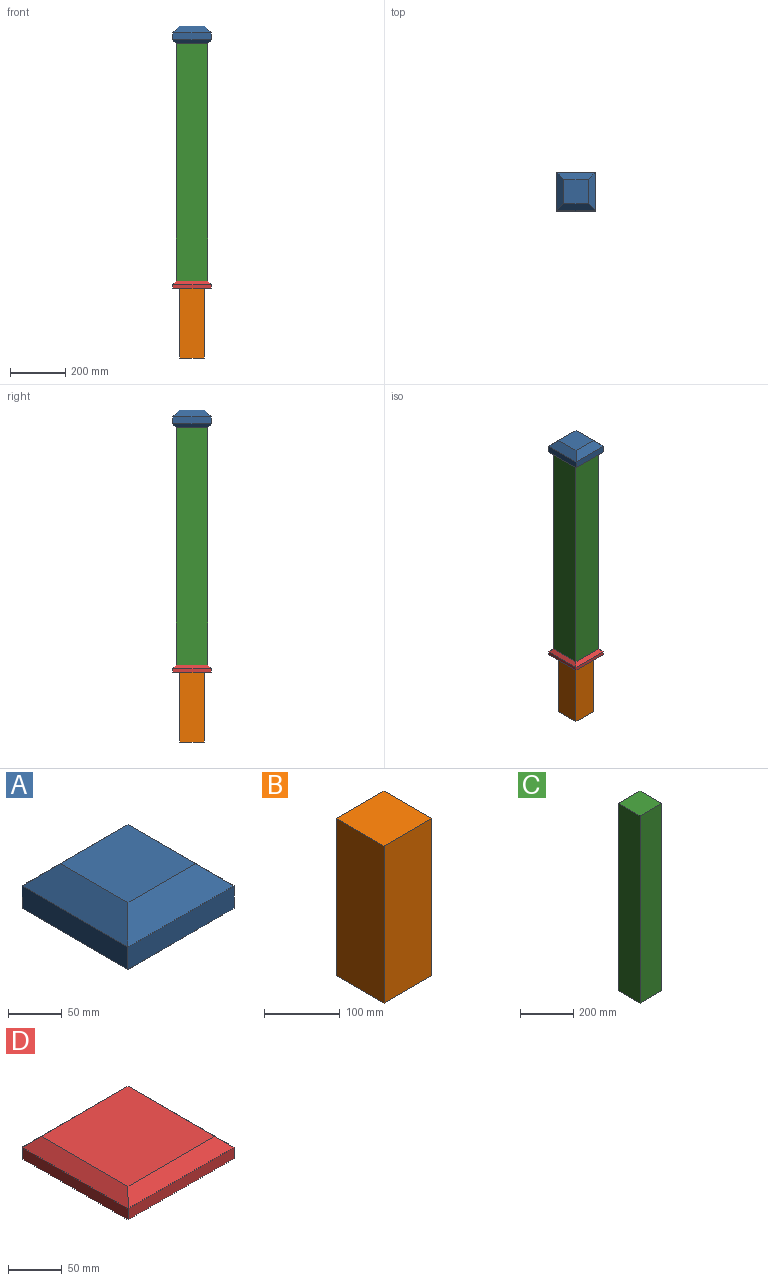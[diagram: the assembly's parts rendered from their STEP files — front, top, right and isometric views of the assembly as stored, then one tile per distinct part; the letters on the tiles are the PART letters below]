
ASSEMBLY  parts=4 mates=3
PART A: 14 faces, bbox 139.7x139.7x63.5 mm
  f0: plane 139.7x25.4mm, normal (1,0,0), area 3548.4mm2, adj f1,f3,f9,f13
  f1: plane 139.7x25.4mm, normal (0,1,0), area 3548.4mm2, adj f0,f2,f7,f11
  f2: plane 139.7x25.4mm, normal (-1,0,0), area 3548.4mm2, adj f1,f3,f6,f10
  f3: plane 139.7x25.4mm, normal (0,-1,0), area 3548.4mm2, adj f0,f2,f8,f12
  f4: plane 88.9x88.9mm, normal (0,0,1), area 7903.2mm2, adj f10,f11,f12,f13
  f5: plane 114.3x114.3mm, normal (0,0,-1), area 13064.5mm2, adj f6,f7,f8,f9
  f6: plane 139.7x12.7mm, normal (-0.71,0,-0.71), area 2281mm2, adj f2,f5,f7,f8
  f7: plane 139.7x12.7mm, normal (0,0.71,-0.71), area 2281mm2, adj f1,f5,f6,f9
  f8: plane 139.7x12.7mm, normal (0,-0.71,-0.71), area 2281mm2, adj f3,f5,f6,f9
  f9: plane 139.7x12.7mm, normal (0.71,0,-0.71), area 2281mm2, adj f0,f5,f7,f8
  f10: plane 139.7x25.4mm, normal (-0.71,0,0.71), area 4105.8mm2, adj f2,f4,f11,f12
  f11: plane 139.7x25.4mm, normal (0,0.71,0.71), area 4105.8mm2, adj f1,f4,f10,f13
  f12: plane 139.7x25.4mm, normal (0,-0.71,0.71), area 4105.8mm2, adj f3,f4,f10,f13
  f13: plane 139.7x25.4mm, normal (0.71,0,0.71), area 4105.8mm2, adj f0,f4,f11,f12
PART B: 6 faces, bbox 88.9x88.9x254 mm
  f0: plane 254x88.9mm, normal (0,-1,0), area 22580.6mm2, adj f1,f3,f4,f5
  f1: plane 254x88.9mm, normal (1,0,0), area 22580.6mm2, adj f0,f2,f4,f5
  f2: plane 254x88.9mm, normal (0,1,0), area 22580.6mm2, adj f1,f3,f4,f5
  f3: plane 254x88.9mm, normal (-1,0,0), area 22580.6mm2, adj f0,f2,f4,f5
  f4: plane 88.9x88.9mm, normal (0,0,1), area 7903.2mm2, adj f0,f1,f2,f3
  f5: plane 88.9x88.9mm, normal (0,0,-1), area 7903.2mm2, adj f0,f1,f2,f3
PART C: 6 faces, bbox 114.3x114.3x863.6 mm
  f0: plane 863.6x114.3mm, normal (-1,0,0), area 98709.5mm2, adj f1,f3,f4,f5
  f1: plane 863.6x114.3mm, normal (0,-1,0), area 98709.5mm2, adj f0,f2,f4,f5
  f2: plane 863.6x114.3mm, normal (1,0,0), area 98709.5mm2, adj f1,f3,f4,f5
  f3: plane 863.6x114.3mm, normal (0,1,0), area 98709.5mm2, adj f0,f2,f4,f5
  f4: plane 114.3x114.3mm, normal (0,0,1), area 13064.5mm2, adj f0,f1,f2,f3
  f5: plane 114.3x114.3mm, normal (0,0,-1), area 13064.5mm2, adj f0,f1,f2,f3
PART D: 10 faces, bbox 139.7x139.7x25.4 mm
  f0: plane 139.7x12.7mm, normal (0,1,0), area 1774.2mm2, adj f1,f3,f5,f7
  f1: plane 139.7x12.7mm, normal (-1,0,0), area 1774.2mm2, adj f0,f2,f5,f6
  f2: plane 139.7x12.7mm, normal (0,-1,0), area 1774.2mm2, adj f1,f3,f5,f8
  f3: plane 139.7x12.7mm, normal (1,0,0), area 1774.2mm2, adj f0,f2,f5,f9
  f4: plane 114.3x114.3mm, normal (0,0,1), area 13064.5mm2, adj f6,f7,f8,f9
  f5: plane 139.7x139.7mm, normal (0,0,-1), area 19516.1mm2, adj f0,f1,f2,f3
  f6: plane 139.7x12.7mm, normal (-0.71,0,0.71), area 2281mm2, adj f1,f4,f7,f8
  f7: plane 139.7x12.7mm, normal (0,0.71,0.71), area 2281mm2, adj f0,f4,f6,f9
  f8: plane 139.7x12.7mm, normal (0,-0.71,0.71), area 2281mm2, adj f2,f4,f6,f9
  f9: plane 139.7x12.7mm, normal (0.71,0,0.71), area 2281mm2, adj f3,f4,f7,f8
PLACE A t=(24.16,144.26,1143)mm
PLACE B at identity
PLACE C t=(-317.65,17.26,279.4)mm
PLACE D t=(-163.65,172.75,254)mm
MATE fastened C.f5 <-> D.f4  axis (0,0,-1) through (-93.8,74.41,279.4)mm
MATE fastened D.f5 <-> B.f4  axis (0,0,-1) through (-93.8,74.41,254)mm
MATE fastened A.f5 <-> C.f4  axis (0,0,-1) through (-93.8,74.41,1143)mm
